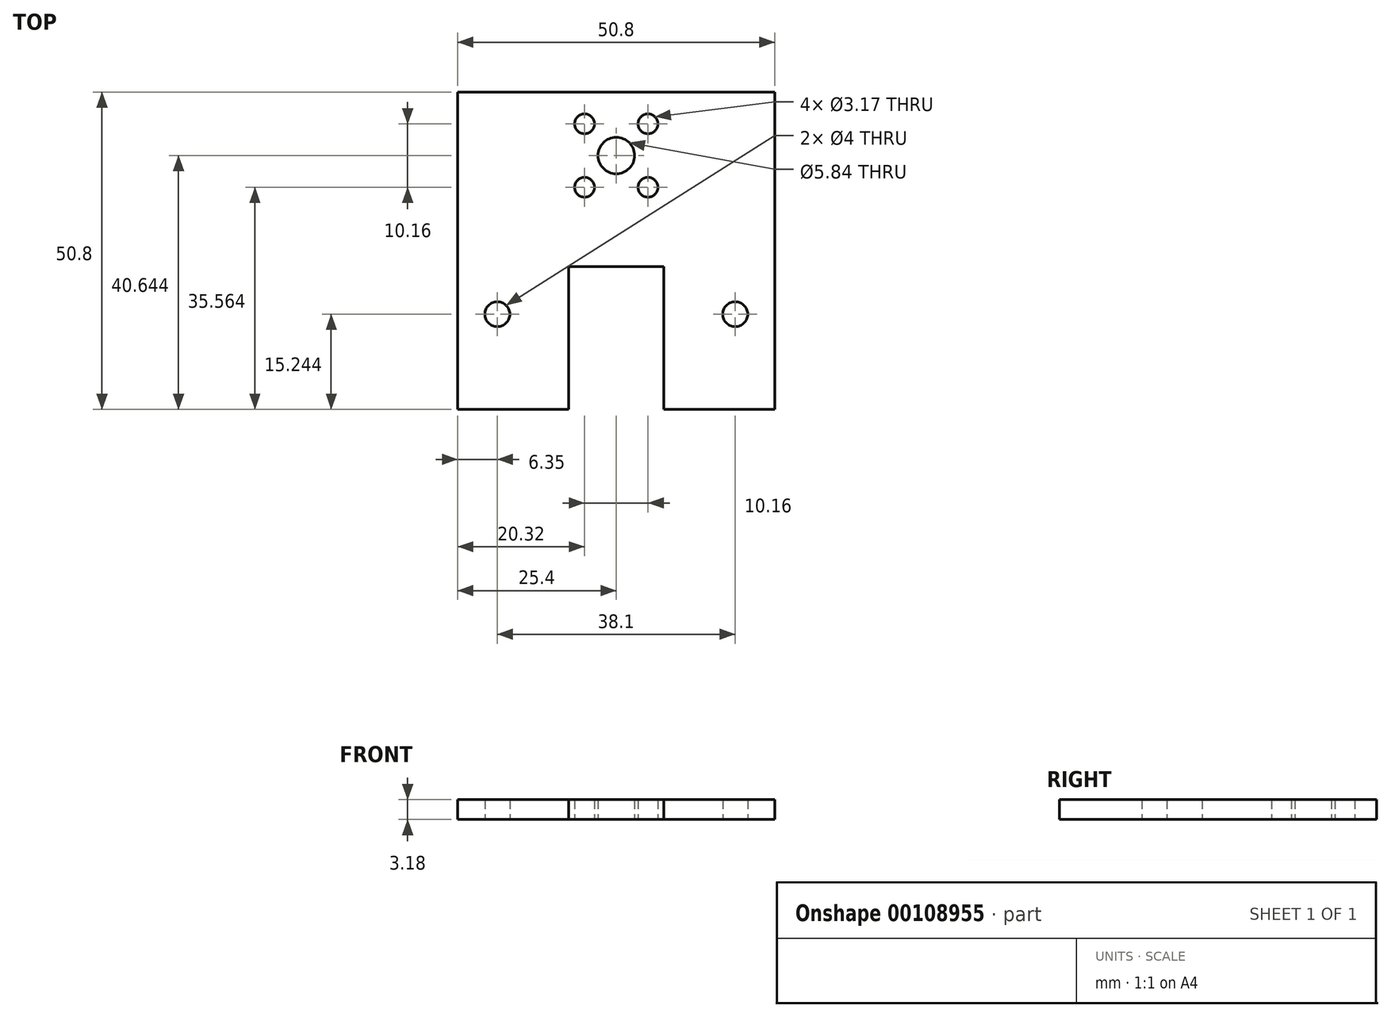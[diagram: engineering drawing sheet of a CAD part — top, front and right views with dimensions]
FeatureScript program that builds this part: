
annotation { "Feature Type Name" : "Feature", "Feature Type Description" : "" }
export const myFeature = defineFeature(function(context is Context, id is Id, definition is map)
    precondition{}
    {
        {
            var Q0;
            Q0=qCreatedBy(makeId("Top.planeOp"),FACE);
            var sketch = newSketch(context, id + "F0", { "sketchPlane" : qUnion([Q0])});
            skLineSegment(sketch, "E0.bottom", {"start": v(-25.4, 25.44) * mm, "end": v(-7.62, 25.44) * mm});
            skLineSegment(sketch, "E0.top", {"start": v(-25.4, 76.24) * mm, "end": v(25.4, 76.24) * mm});
            skLineSegment(sketch, "E0.left", {"start": v(-25.4, 25.44) * mm, "end": v(-25.4, 76.24) * mm});
            skLineSegment(sketch, "E0.right", {"start": v(25.4, 25.44) * mm, "end": v(25.4, 76.24) * mm});
            skCircle(sketch, "E1", {"center": v(0, 66.08) * mm, "radius": 2.92 * mm});
            skCircle(sketch, "E2", {"center": v(-5.08, 71.16) * mm, "radius": 1.59 * mm});
            skCircle(sketch, "E3", {"center": v(-5.08, 61) * mm, "radius": 1.59 * mm});
            skCircle(sketch, "E4", {"center": v(5.08, 71.16) * mm, "radius": 1.59 * mm});
            skCircle(sketch, "E5", {"center": v(5.08, 61) * mm, "radius": 1.59 * mm});
            skLineSegment(sketch, "E6.bottom", {"start": v(-7.62, 48.3) * mm, "end": v(7.62, 48.3) * mm});
            skLineSegment(sketch, "E6.left", {"start": v(-7.62, 48.3) * mm, "end": v(-7.62, 25.44) * mm});
            skLineSegment(sketch, "E6.right", {"start": v(7.62, 48.3) * mm, "end": v(7.62, 25.44) * mm});
            skCircle(sketch, "E7", {"center": v(19.05, 40.68) * mm, "radius": 2 * mm});
            skCircle(sketch, "E8", {"center": v(-19.05, 40.68) * mm, "radius": 2 * mm});
            skPoint(sketch, "E9", {"position": v(0, 76.24) * mm});
            skPoint(sketch, "E10", {"position": v(0, 48.3) * mm});
            skLineSegment(sketch, "E11.trimOffspring", {"start": v(7.62, 25.44) * mm, "end": v(25.4, 25.44) * mm});
            skSolve(sketch);
        }
        {
            var Q0;
            Q0=makeQuery(id+"F0.imprint","IMPRINT",FACE,{"disambiguationData":[TD([[makeQuery(id+"F0.imprint","IMPRINT",EDGE,{"derivedFrom":sQuery(id+"F0.wireOp",EDGE,"2006bb52-2d54-4f0e-ba05-1ae574e5513b")}),1.0]])]});
            var Q1;
            Q1=makeQuery(id+"F0.imprint","IMPRINT",FACE,{"disambiguationData":[TD([[makeQuery(id+"F0.imprint","IMPRINT",EDGE,{"derivedFrom":sQuery(id+"F0.wireOp",EDGE,"E0.top")}),-1.0]])]});
            extrude(context, id + "F1", {"entities" : qUnion([Q0, Q1]), "depth" : 3.17 * mm});
        }
    });
